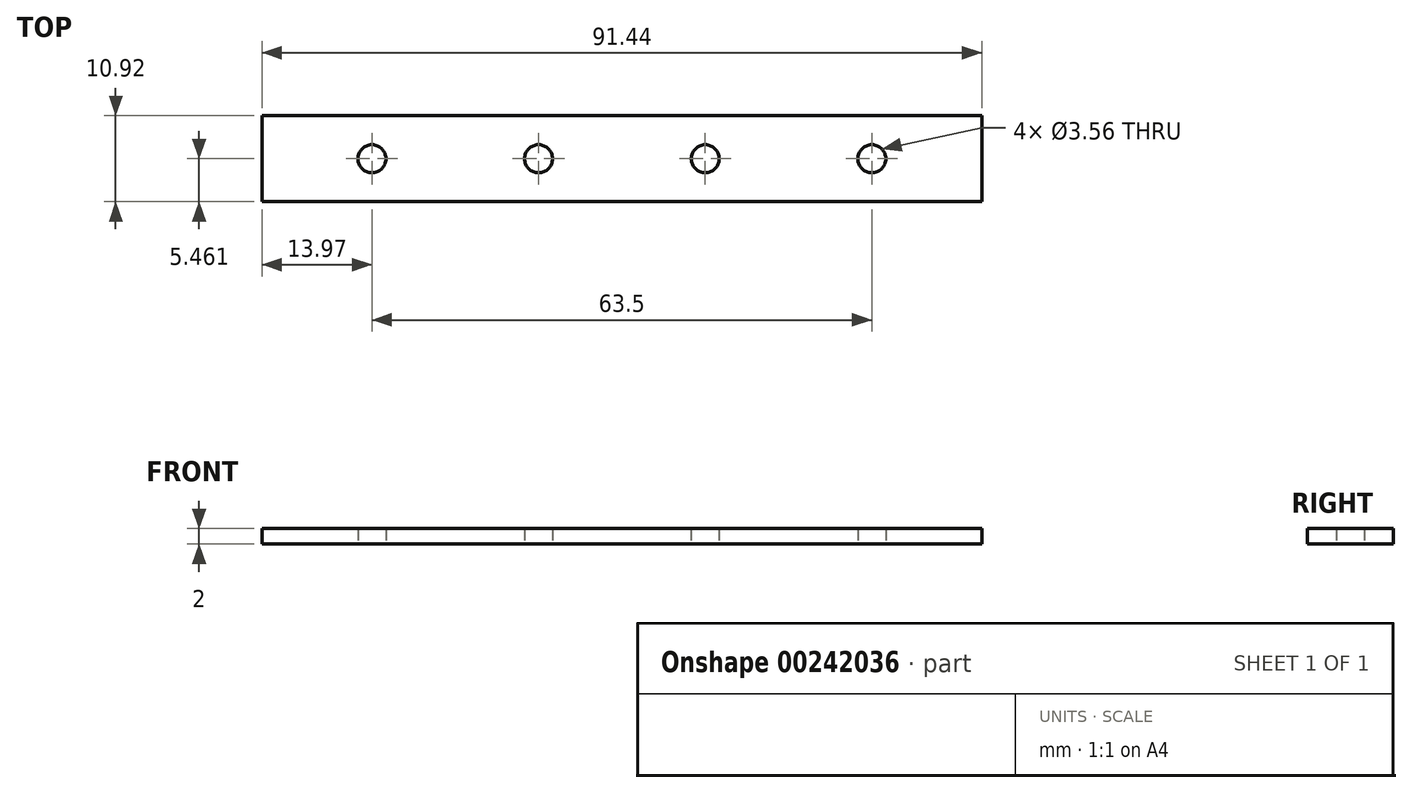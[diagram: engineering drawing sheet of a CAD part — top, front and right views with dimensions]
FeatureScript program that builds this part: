
annotation { "Feature Type Name" : "Feature", "Feature Type Description" : "" }
export const myFeature = defineFeature(function(context is Context, id is Id, definition is map)
    precondition{}
    {
        {
            var Q0;
            Q0=qCreatedBy(makeId("Top.planeOp"),FACE);
            var sketch = newSketch(context, id + "F0", { "sketchPlane" : qUnion([Q0])});
            skLineSegment(sketch, "E0.bottom", {"start": v(0, 0) * mm, "end": v(91.44, 0) * mm});
            skLineSegment(sketch, "E0.top", {"start": v(0, 10.92) * mm, "end": v(91.44, 10.92) * mm});
            skLineSegment(sketch, "E0.left", {"start": v(0, 0) * mm, "end": v(0, 10.92) * mm});
            skLineSegment(sketch, "E0.right", {"start": v(91.44, 0) * mm, "end": v(91.44, 10.92) * mm});
            skLineSegment(sketch, "E1", {"start": v(45.72, 10.92) * mm, "end": v(45.72, 0) * mm, "construction": true});
            skCircle(sketch, "E2", {"center": v(13.97, 5.46) * mm, "radius": 1.78 * mm});
            skLineSegment(sketch, "E3", {"start": v(0, 5.46) * mm, "end": v(45.72, 5.46) * mm, "construction": true});
            skCircle(sketch, "E4.1.0.0", {"center": v(35.14, 5.46) * mm, "radius": 1.78 * mm});
            skCircle(sketch, "E4.2.0.0", {"center": v(56.3, 5.46) * mm, "radius": 1.78 * mm});
            skCircle(sketch, "E4.3.0.0", {"center": v(77.47, 5.46) * mm, "radius": 1.78 * mm});
            skLineSegment(sketch, "E4.direction1", {"start": v(13.97, 5.46) * mm, "end": v(35.14, 5.46) * mm, "construction": true});
            skSolve(sketch);
        }
        {
            var Q0;
            Q0 = qSketchRegion(id + "F0", true);
            extrude(context, id + "F1", {"entities" : qUnion([Q0]), "depth" : 2 * mm});
        }
    });
